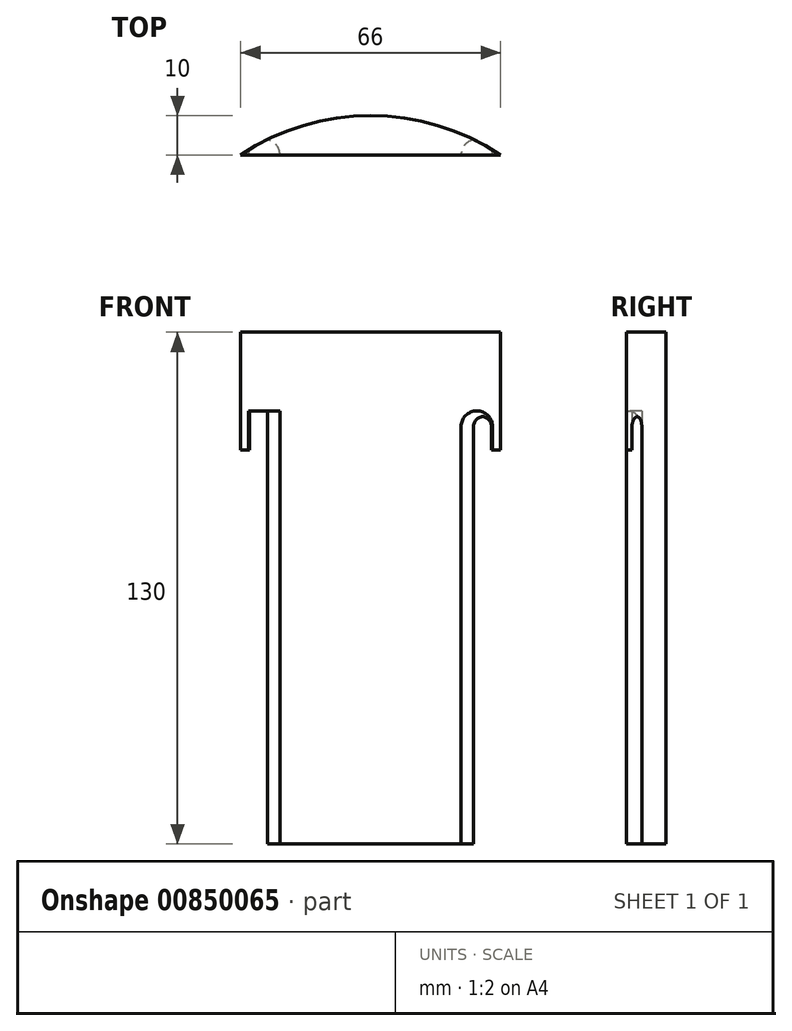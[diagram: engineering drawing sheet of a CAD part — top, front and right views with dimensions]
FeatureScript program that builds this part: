
annotation { "Feature Type Name" : "Feature", "Feature Type Description" : "" }
export const myFeature = defineFeature(function(context is Context, id is Id, definition is map)
    precondition{}
    {
        {
            var Q0;
            Q0=qCreatedBy(makeId("Top.planeOp"),FACE);
            var sketch = newSketch(context, id + "F0", { "sketchPlane" : qUnion([Q0])});
            skLineSegment(sketch, "E0", {"start": v(0, 0) * mm, "end": v(66, 0) * mm});
            skArc(sketch, "E1", {"start": v(66, 0) * mm, "mid": v(33, 10) * mm, "end": v(0, 0) * mm});
            skSolve(sketch);
        }
        {
            var Q0;
            Q0=makeQuery(id+"F0.imprint","IMPRINT",FACE,{"disambiguationData":[TD([[makeQuery(id+"F0.imprint","IMPRINT",EDGE,{"derivedFrom":sQuery(id+"F0.wireOp",EDGE,"E0")}),1.0]])]});
            extrude(context, id + "F1", {"entities" : qUnion([Q0]), "depth" : 130 * mm, "offsetDistance" : 25 * mm});
        }
        {
            var Q0;
            Q0=makeQuery(id+"F1.opExtrude","CAP_FACE",FACE,{"disambiguationData":[OSD([sQuery(id+"F0.wireOp",EDGE,"E0"),sQuery(id+"F0.wireOp",EDGE,"E1")])],"isStart":true});
            var sketch = newSketch(context, id + "F2", { "sketchPlane" : qUnion([Q0])});
            skLineSegment(sketch, "E2", {"start": v(33, 0) * mm, "end": v(56, 0) * mm});
            skLineSegment(sketch, "E3", {"start": v(56, 0) * mm, "end": v(60, 0) * mm});
            skCircle(sketch, "E4", {"center": v(60, 0) * mm, "radius": 4 * mm});
            skLineSegment(sketch, "E5", {"start": v(33, 0) * mm, "end": v(10, 0) * mm});
            skLineSegment(sketch, "E6", {"start": v(10, 0) * mm, "end": v(6, 0) * mm});
            skCircle(sketch, "E7", {"center": v(6, 0) * mm, "radius": 4 * mm});
            skSolve(sketch);
        }
        {
            var Q0;
            {var subQ0=sQuery(id+"F2.wireOp",EDGE,"E3");Q0=makeQuery(id+"F2.imprint","IMPRINT",FACE,{"disambiguationData":[TD([[makeQuery(id+"F2.imprint","IMPRINT",EDGE,{"derivedFrom":subQ0}),1.0]])]});}
            var Q1;
            {var subQ5=sQuery(id+"F2.wireOp",EDGE,"E3");Q1=makeQuery(id+"F2.imprint","IMPRINT",FACE,{"disambiguationData":[TD([[makeQuery(id+"F2.imprint","IMPRINT",EDGE,{"derivedFrom":subQ5}),-1.0]])]});}
            var Q2;
            {var subQ0=sQuery(id+"F2.wireOp",EDGE,"E4");var subQ1=makeQuery(id+"F1.opExtrude","CAP_EDGE",EDGE,{"disambiguationData":[OSD([sQuery(id+"F0.wireOp",EDGE,"E1")])],"isStart":true});var subQ2=makeQuery(id+"F2.imprint","INTERSECT",VERTEX,{"disambiguationData":[OD(0.0)],"derivedFrom":[subQ1,subQ0]});Q2=makeQuery(id+"F2.imprint","IMPRINT",FACE,{"disambiguationData":[TD([[makeQuery(id+"F2.imprint","IMPRINT",EDGE,{"disambiguationData":[TD([[subQ2,-1.0]])],"derivedFrom":subQ0}),1.0]])]});}
            var Q3;
            {var subQ0=sQuery(id+"F2.wireOp",EDGE,"E6");Q3=makeQuery(id+"F2.imprint","IMPRINT",FACE,{"disambiguationData":[TD([[makeQuery(id+"F2.imprint","IMPRINT",EDGE,{"derivedFrom":subQ0}),1.0]])]});}
            var Q4;
            {var subQ0=sQuery(id+"F2.wireOp",EDGE,"E6");Q4=makeQuery(id+"F2.imprint","IMPRINT",FACE,{"disambiguationData":[TD([[makeQuery(id+"F2.imprint","IMPRINT",EDGE,{"derivedFrom":subQ0}),-1.0]])]});}
            extrude(context, id + "F3", {"entities" : qUnion([Q0, Q1, Q2, Q3, Q4]), "operationType" : NewBodyOperationType.REMOVE, "oppositeDirection" : true, "depth" : 110 * mm, "offsetDistance" : 25 * mm});
        }
        {
            var Q0;
            {var subQ0=sQuery(id+"F0.wireOp",EDGE,"E0");var subQ1=sQuery(id+"F0.wireOp",EDGE,"E1");Q0=makeQuery(id+"F3.boolean.opBoolean","SPLIT",FACE,{"disambiguationData":[TD([makeQuery(id+"F1.opExtrude","SWEPT_FACE",FACE,{"disambiguationData":[OSD([subQ0])]}),makeQuery(id+"F1.opExtrude","SWEPT_FACE",FACE,{"disambiguationData":[OSD([subQ1])]}),makeQuery(id+"F3.opExtrude","SWEPT_FACE",FACE,{"disambiguationData":[OSD([sQuery(id+"F2.wireOp",EDGE,"E4")])]})])],"derivedFrom":makeQuery(id+"F1.opExtrude","CAP_FACE",FACE,{"disambiguationData":[OSD([subQ0,subQ1])],"isStart":true})});}
            extrude(context, id + "F4", {"entities" : qUnion([Q0]), "operationType" : NewBodyOperationType.REMOVE, "oppositeDirection" : true, "depth" : 100 * mm, "offsetDistance" : 25 * mm});
        }
        {
            var Q0;
            {var subQ0=sQuery(id+"F0.wireOp",EDGE,"E0");var subQ1=sQuery(id+"F0.wireOp",EDGE,"E1");Q0=makeQuery(id+"F3.boolean.opBoolean","SPLIT",FACE,{"disambiguationData":[TD([makeQuery(id+"F1.opExtrude","SWEPT_FACE",FACE,{"disambiguationData":[OSD([subQ0])]}),makeQuery(id+"F1.opExtrude","SWEPT_FACE",FACE,{"disambiguationData":[OSD([subQ1])]}),makeQuery(id+"F3.opExtrude","SWEPT_FACE",FACE,{"disambiguationData":[OSD([sQuery(id+"F2.wireOp",EDGE,"E7")])]})])],"derivedFrom":makeQuery(id+"F1.opExtrude","CAP_FACE",FACE,{"disambiguationData":[OSD([subQ0,subQ1])],"isStart":true})});}
            extrude(context, id + "F5", {"entities" : qUnion([Q0]), "operationType" : NewBodyOperationType.REMOVE, "oppositeDirection" : true, "depth" : 100 * mm, "offsetDistance" : 25 * mm});
        }
        {
            var Q0;
            Q0=makeQuery(id+"F3.boolean.opBoolean","COPY",EDGE,{"disambiguationData":[OD(0.0)],"derivedFrom":makeQuery(id+"F3.opExtrude","CAP_EDGE",EDGE,{"disambiguationData":[OSD([sQuery(id+"F2.wireOp",EDGE,"E4")])],"isStart":false})});
            fillet(context, id + "F6", {"entities" : qUnion([Q0]), "radius" : 4 * mm, "tangentPropagation" : true, "allowEdgeOverflow" : false});
        }
    });
